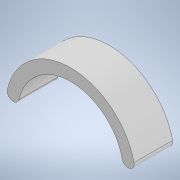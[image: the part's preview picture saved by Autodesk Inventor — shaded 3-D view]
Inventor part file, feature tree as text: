
AUTODESK INVENTOR PART (.ipt)
format: ipt  version: 2020 (Build 240168000, 168)  size: 103,936 bytes
history: native  units: in
note: dims shown in document units (in); Inventor stores cm internally (conversion verified against a paired STEP export)
features: extrude x1, sketch x1
ambient origin geometry x8: Origin, YZ Plane, XZ Plane, XY Plane, X Axis, Y Axis, Z Axis, Center Point
bodies: Solid1 (feature_tree)
feature tree (2):
  extrude  "Extrusion1"  Depth=1.0257in
  sketch  "Sketch1"  dims[d0=0.1165in d1=1.0257in d2=0.25in d3=0.75in d4=0.0in]
